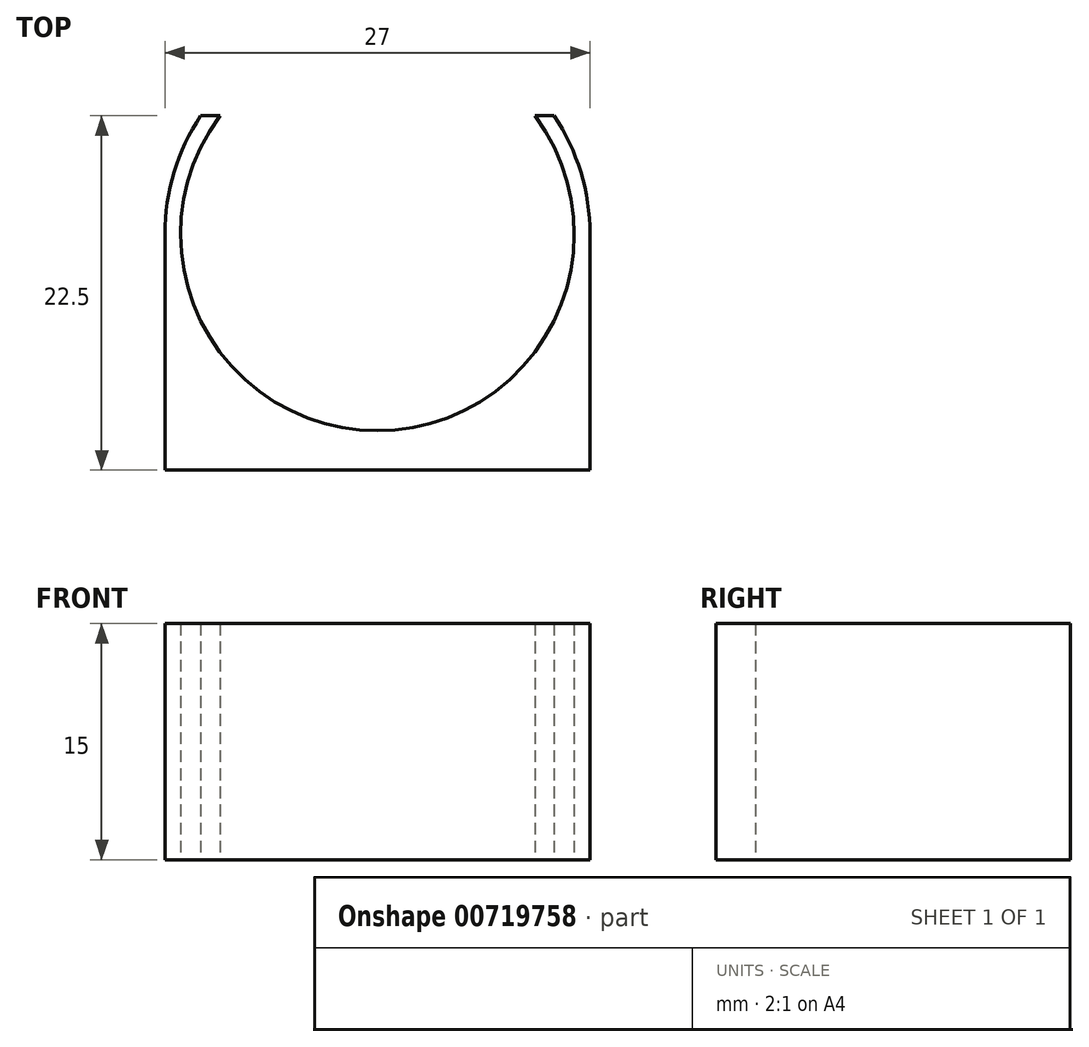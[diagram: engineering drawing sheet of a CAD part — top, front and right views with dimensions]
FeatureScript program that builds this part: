
annotation { "Feature Type Name" : "Feature", "Feature Type Description" : "" }
export const myFeature = defineFeature(function(context is Context, id is Id, definition is map)
    precondition{}
    {
        {
            var Q0;
            Q0=qCreatedBy(makeId("Top.planeOp"),FACE);
            var sketch = newSketch(context, id + "F0", { "sketchPlane" : qUnion([Q0])});
            skArc(sketch, "E0", {"start": v(3.5, 22.5) * mm, "mid": v(13.5, 2.5) * mm, "end": v(23.5, 22.5) * mm});
            skArc(sketch, "E1", {"start": v(2.28, 22.5) * mm, "mid": v(0.58, 18.92) * mm, "end": v(0, 15) * mm});
            skLineSegment(sketch, "E2", {"start": v(0, 15) * mm, "end": v(0, 0) * mm});
            skLineSegment(sketch, "E3", {"start": v(2.28, 22.5) * mm, "end": v(24.72, 22.5) * mm});
            skLineSegment(sketch, "E4", {"start": v(27, 15) * mm, "end": v(27, 0) * mm});
            skLineSegment(sketch, "E5", {"start": v(27, 0) * mm, "end": v(0, 0) * mm});
            skArc(sketch, "E6.trimOffspring", {"start": v(27, 15) * mm, "mid": v(26.42, 18.92) * mm, "end": v(24.72, 22.5) * mm});
            skSolve(sketch);
        }
        {
            var Q0;
            {var subQ1=sQuery(id+"F0.wireOp",EDGE,"E0");Q0=makeQuery(id+"F0.imprint","IMPRINT",FACE,{"disambiguationData":[TD([[makeQuery(id+"F0.imprint","IMPRINT",EDGE,{"derivedFrom":subQ1}),-1.0]])]});}
            extrude(context, id + "F1", {"entities" : qUnion([Q0]), "depth" : 15 * mm, "offsetDistance" : 25 * mm});
        }
    });
